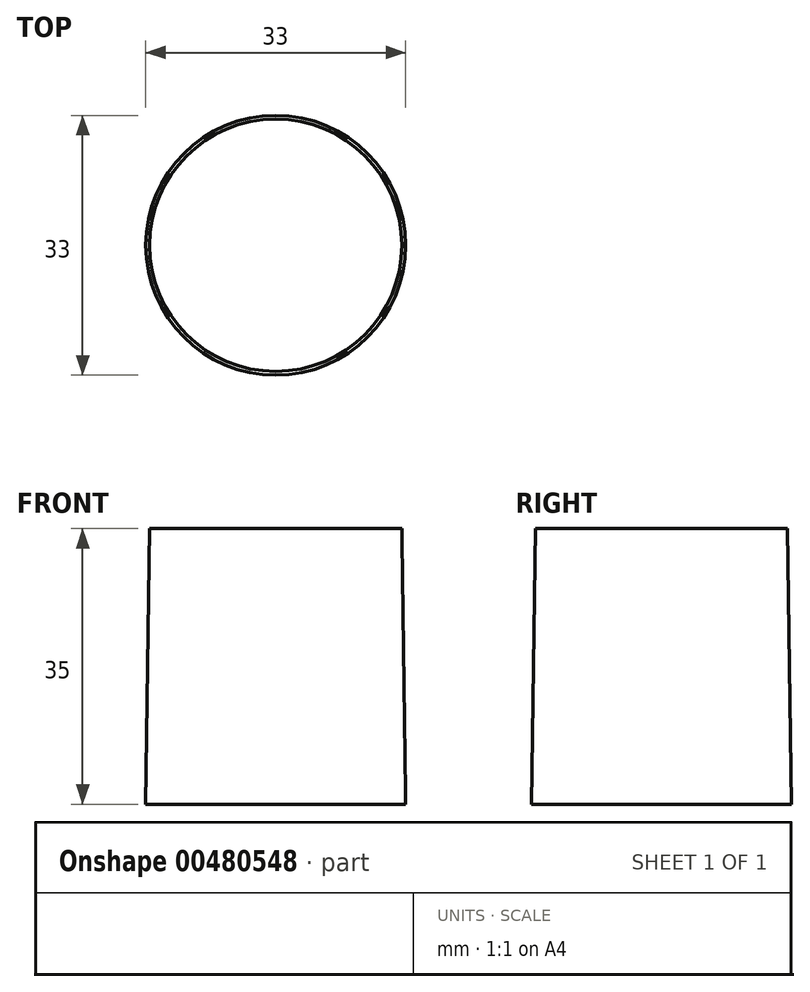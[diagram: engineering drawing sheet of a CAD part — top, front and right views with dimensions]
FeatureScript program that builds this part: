
annotation { "Feature Type Name" : "Feature", "Feature Type Description" : "" }
export const myFeature = defineFeature(function(context is Context, id is Id, definition is map)
    precondition{}
    {
        {
            assignVariable(context, id + "F0", {"name" : "Length1stPipe", "anyValue" : 35});
        }
        {
            var Q0;
            Q0=qCreatedBy(makeId("Top.planeOp"),FACE);
            var sketch = newSketch(context, id + "F1", { "sketchPlane" : qUnion([Q0])});
            skCircle(sketch, "E0", {"center": v(0, 0) * mm, "radius": 16.5 * mm});
            skSolve(sketch);
        }
        {
            var Q0;
            Q0=qCreatedBy(makeId("Top.planeOp"),FACE);
            cPlane(context, id + "F2", {"entities" : qUnion([Q0]), "cplaneType" : CPlaneType.OFFSET, "offset" : (getVariable(context, 'Length1stPipe')) * mm, "width" : 150 * mm, "height" : 150 * mm});
        }
        {
            var Q0;
            Q0=qCreatedBy(id+"F2.planeOp",FACE);
            var sketch = newSketch(context, id + "F3", { "sketchPlane" : qUnion([Q0])});
            skCircle(sketch, "E1", {"center": v(0, 0) * mm, "radius": 16.02 * mm});
            skSolve(sketch);
        }
        {
            var Q0;
            Q0=makeQuery(id+"F1.imprint","IMPRINT",FACE,{"disambiguationData":[TD([[makeQuery(id+"F1.imprint","IMPRINT",EDGE,{"derivedFrom":sQuery(id+"F1.wireOp",EDGE,"E0")}),1.0]])]});
            var Q1;
            Q1=makeQuery(id+"F3.imprint","IMPRINT",FACE,{"disambiguationData":[TD([[makeQuery(id+"F3.imprint","IMPRINT",EDGE,{"derivedFrom":sQuery(id+"F3.wireOp",EDGE,"E1")}),1.0]])]});
            loft(context, id + "F4", {"sheetProfilesArray" : [{ "sheetProfileEntities" : qUnion([Q0]) }, { "sheetProfileEntities" : qUnion([Q1]) }]});
        }
    });
